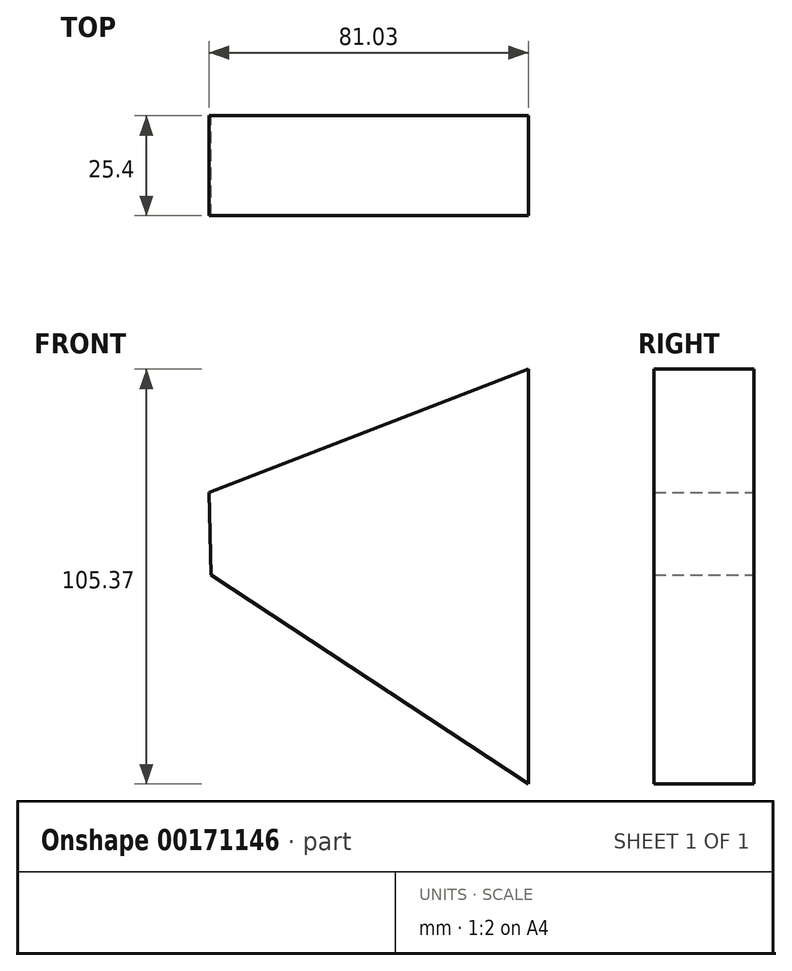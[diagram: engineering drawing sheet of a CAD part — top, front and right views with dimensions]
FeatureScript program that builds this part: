
annotation { "Feature Type Name" : "Feature", "Feature Type Description" : "" }
export const myFeature = defineFeature(function(context is Context, id is Id, definition is map)
    precondition{}
    {
        {
            var Q0;
            Q0=qCreatedBy(makeId("Front.planeOp"),FACE);
            var sketch = newSketch(context, id + "F0", { "sketchPlane" : qUnion([Q0])});
            skLineSegment(sketch, "E0", {"start": v(-35.56, 34.87) * mm, "end": v(45.47, 66.23) * mm});
            skLineSegment(sketch, "E1", {"start": v(45.47, 66.23) * mm, "end": v(45.47, -39.14) * mm});
            skLineSegment(sketch, "E2", {"start": v(45.47, -39.14) * mm, "end": v(-35.13, 13.88) * mm});
            skLineSegment(sketch, "E3", {"start": v(-35.13, 13.88) * mm, "end": v(-35.56, 34.87) * mm});
            skSolve(sketch);
        }
        {
            var Q0;
            Q0 = qSketchRegion(id + "F0", true);
            extrude(context, id + "F1", {"entities" : qUnion([Q0]), "depth" : 25.4 * mm});
        }
    });
